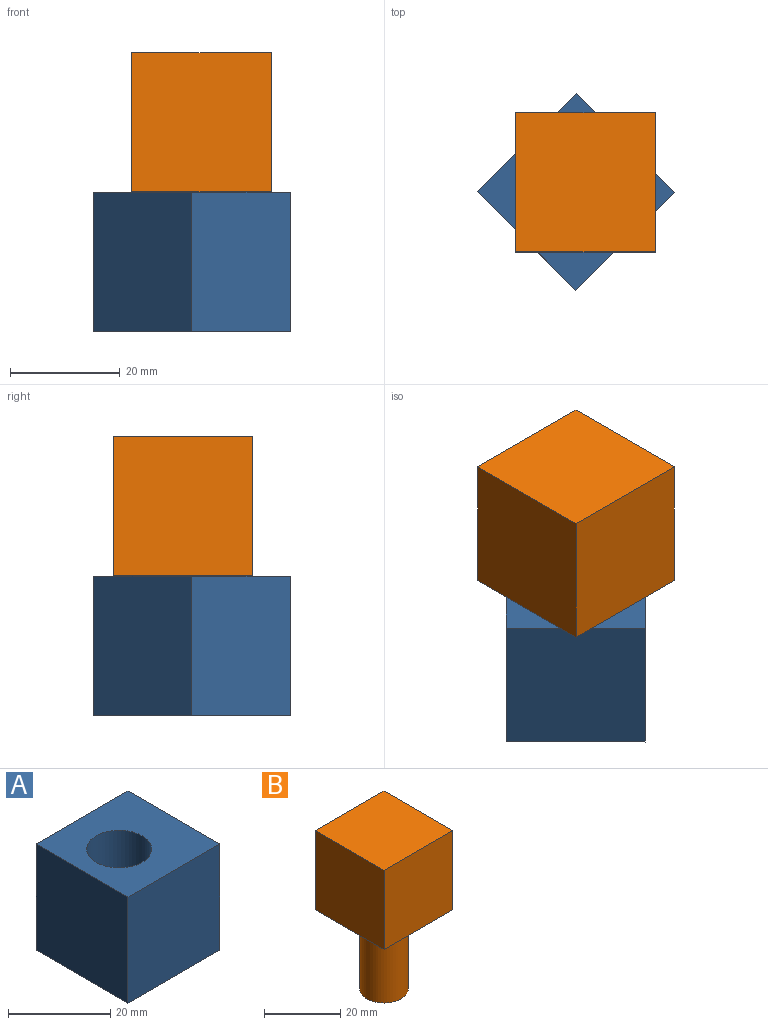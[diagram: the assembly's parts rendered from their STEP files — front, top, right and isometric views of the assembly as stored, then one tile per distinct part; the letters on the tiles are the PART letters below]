
ASSEMBLY  parts=2 mates=2
PART A: 7 faces, bbox 25.4x25.4x25.4 mm
  f0: plane 25.4x25.4mm, normal (1,0,0), area 645.2mm2, adj f1,f3,f4,f5
  f1: plane 25.4x25.4mm, normal (0,1,0), area 645.2mm2, adj f0,f2,f4,f5
  f2: plane 25.4x25.4mm, normal (-1,0,0), area 645.2mm2, adj f1,f3,f4,f5
  f3: plane 25.4x25.4mm, normal (0,-1,0), area 645.2mm2, adj f0,f2,f4,f5
  f4: plane 25.4x25.4mm, normal (0,0,1), area 518.5mm2, adj f0,f1,f2,f3,f6
  f5: plane 25.4x25.4mm, normal (0,0,-1), area 518.5mm2, adj f0,f1,f2,f3,f6
  f6: cylinder r=6.35mm len=25.4mm, axis (0,0,1), area 1013.4mm2, adj f4,f5
PART B: 8 faces, bbox 25.4x25.4x50.8 mm
  f0: plane 25.4x25.4mm, normal (-1,0,0), area 645.2mm2, adj f1,f3,f4,f5
  f1: plane 25.4x25.4mm, normal (0,-1,0), area 645.2mm2, adj f0,f2,f4,f5
  f2: plane 25.4x25.4mm, normal (1,0,0), area 645.2mm2, adj f1,f3,f4,f5
  f3: plane 25.4x25.4mm, normal (0,1,0), area 645.2mm2, adj f0,f2,f4,f5
  f4: plane 25.4x25.4mm, normal (0,0,1), area 645.2mm2, adj f0,f1,f2,f3
  f5: plane 25.4x25.4mm, normal (0,0,-1), area 518.5mm2, adj f0,f1,f2,f3,f6
  f6: cylinder r=6.35mm len=25.4mm, axis (0,0,1), area 1013.4mm2, adj f5,f7
  f7: plane 12.7x12.7mm, normal (0,0,-1), area 126.7mm2, adj f6
PLACE A rot(axis=(0,0,-1),135.3deg) t=(-3.82,0.58,-18.27)mm
PLACE B t=(-3.82,0.58,7.13)mm fixed
MATE planar B.f6 <-> A.f4  axis (0,0,-1) through (-3.82,0.58,7.13)mm
MATE cylindrical A.f6 <-> B.f6  axis (0,0,-1) through (-3.82,0.58,-18.27)mm
